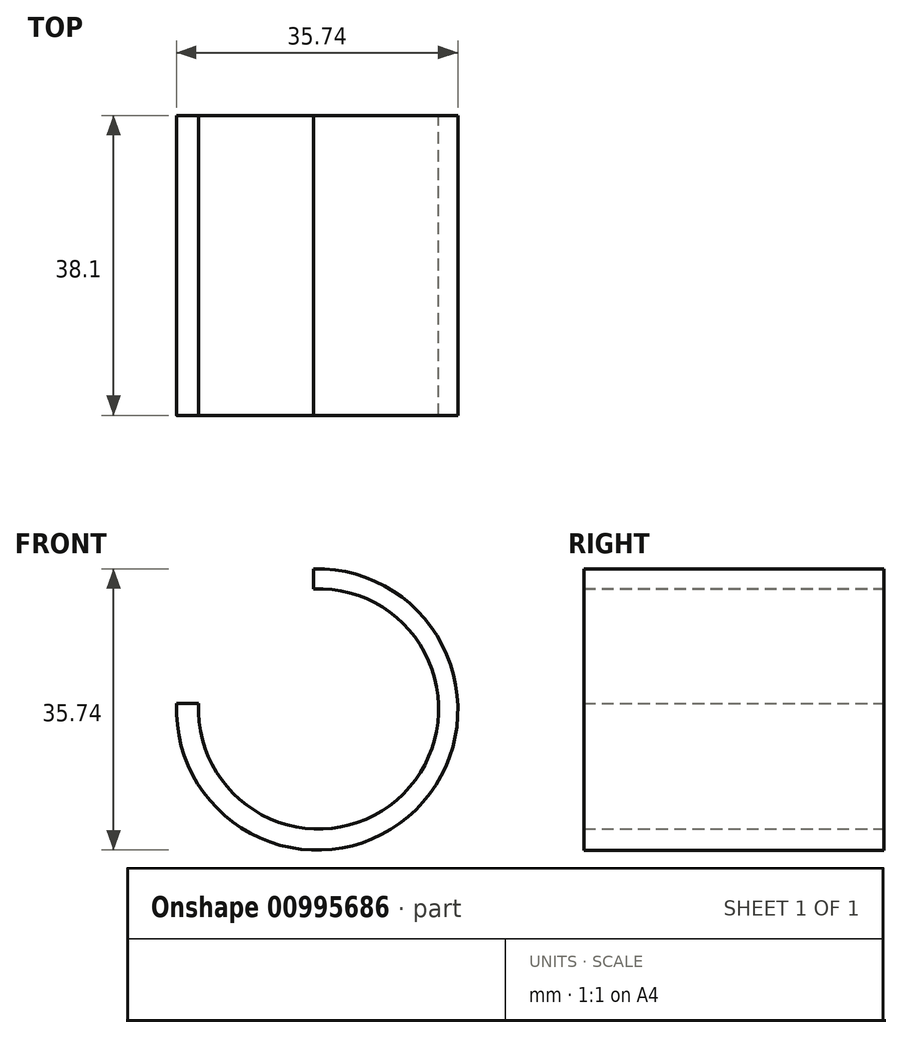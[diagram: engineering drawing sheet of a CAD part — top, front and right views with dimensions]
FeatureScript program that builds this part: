
annotation { "Feature Type Name" : "Feature", "Feature Type Description" : "" }
export const myFeature = defineFeature(function(context is Context, id is Id, definition is map)
    precondition{}
    {
        {
            var Q0;
            Q0=qCreatedBy(makeId("Front.planeOp"),FACE);
            var sketch = newSketch(context, id + "F0", { "sketchPlane" : qUnion([Q0])});
            skArc(sketch, "E0", {"start": v(-17.41, 0) * mm, "mid": v(12.97, -13.48) * mm, "end": v(0, 17.12) * mm});
            skArc(sketch, "E1", {"start": v(-14.64, 0) * mm, "mid": v(11.4, -11.47) * mm, "end": v(0, 14.6) * mm});
            skLineSegment(sketch, "E2", {"start": v(0, 17.12) * mm, "end": v(0, 14.6) * mm});
            skLineSegment(sketch, "E3", {"start": v(-17.41, 0) * mm, "end": v(-14.64, 0) * mm});
            skSolve(sketch);
        }
        {
            var Q0;
            Q0 = qSketchRegion(id + "F0", true);
            extrude(context, id + "F1", {"entities" : qUnion([Q0]), "depth" : 38.1 * mm, "offsetDistance" : 25.4 * mm});
        }
    });
